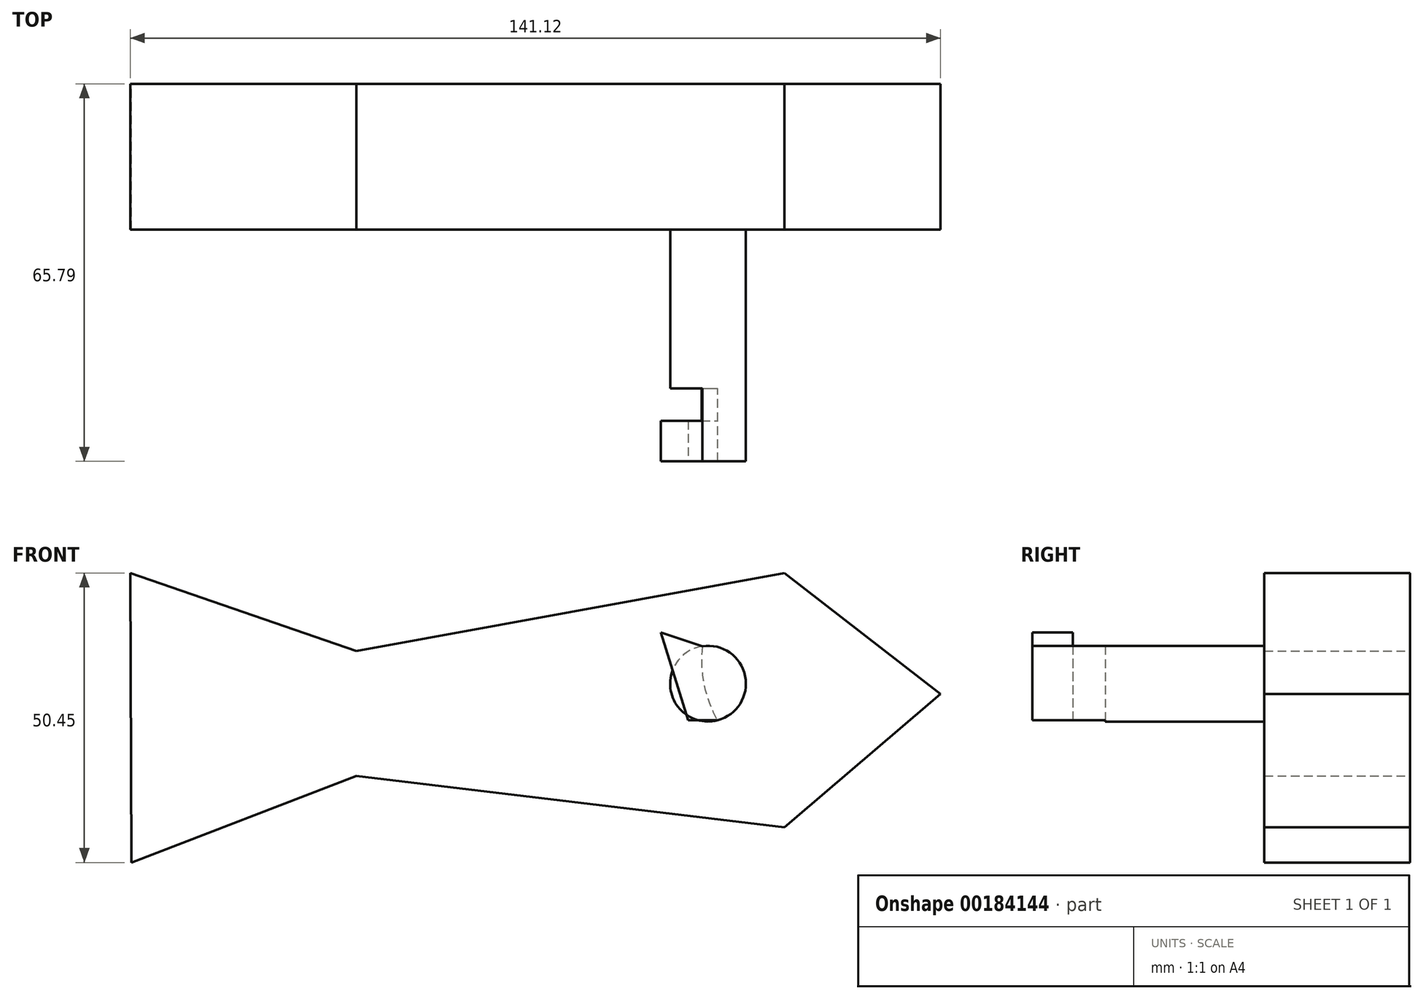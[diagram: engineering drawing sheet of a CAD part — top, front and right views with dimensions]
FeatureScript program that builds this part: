
annotation { "Feature Type Name" : "Feature", "Feature Type Description" : "" }
export const myFeature = defineFeature(function(context is Context, id is Id, definition is map)
    precondition{}
    {
        {
            var Q0;
            Q0=qCreatedBy(makeId("Front.planeOp"),FACE);
            var sketch = newSketch(context, id + "F0", { "sketchPlane" : qUnion([Q0])});
            skLineSegment(sketch, "E0", {"start": v(-76.04, -11.03) * mm, "end": v(-36.69, -24.63) * mm});
            skLineSegment(sketch, "E1", {"start": v(-36.69, -24.63) * mm, "end": v(37.9, -11.03) * mm});
            skLineSegment(sketch, "E2", {"start": v(37.9, -11.03) * mm, "end": v(65.08, -32.1) * mm});
            skLineSegment(sketch, "E3", {"start": v(65.08, -32.1) * mm, "end": v(37.9, -55.37) * mm});
            skLineSegment(sketch, "E4", {"start": v(37.9, -55.37) * mm, "end": v(-36.69, -46.38) * mm});
            skLineSegment(sketch, "E5", {"start": v(-36.69, -46.38) * mm, "end": v(-75.87, -61.48) * mm});
            skLineSegment(sketch, "E6", {"start": v(-76.04, -11.03) * mm, "end": v(-75.87, -61.48) * mm});
            skCircle(sketch, "E7", {"center": v(26.42, -32.28) * mm, "radius": 4.76 * mm});
            skSolve(sketch);
        }
        {
            var Q0;
            Q0=makeQuery(id+"F0.imprint","IMPRINT",FACE,{"disambiguationData":[TD([[makeQuery(id+"F0.imprint","IMPRINT",EDGE,{"derivedFrom":sQuery(id+"F0.wireOp",EDGE,"E0")}),-1.0]])]});
            var Q1;
            Q1=makeQuery(id+"F0.imprint","IMPRINT",FACE,{"disambiguationData":[TD([[makeQuery(id+"F0.imprint","IMPRINT",EDGE,{"derivedFrom":sQuery(id+"F0.wireOp",EDGE,"E7")}),1.0]])]});
            extrude(context, id + "F1", {"entities" : qUnion([Q0, Q1]), "depth" : 25.4 * mm});
        }
        {
            var Q0;
            Q0=makeQuery(id+"F1.opExtrude","CAP_FACE",FACE,{"disambiguationData":[OSD([sQuery(id+"F0.wireOp",EDGE,"E0"),sQuery(id+"F0.wireOp",EDGE,"E1"),sQuery(id+"F0.wireOp",EDGE,"E2"),sQuery(id+"F0.wireOp",EDGE,"E3"),sQuery(id+"F0.wireOp",EDGE,"E4"),sQuery(id+"F0.wireOp",EDGE,"E5"),sQuery(id+"F0.wireOp",EDGE,"E6")])],"isStart":false});
            var sketch = newSketch(context, id + "F2", { "sketchPlane" : qUnion([Q0])});
            skPoint(sketch, "E8.first.point", {"position": v(20.26, -28.29) * mm});
            skPoint(sketch, "E8.second.point", {"position": v(35, -35.2) * mm});
            skPoint(sketch, "E8.third.point", {"position": v(33.42, -27.48) * mm});
            skCircle(sketch, "E9", {"center": v(24.57, -30.3) * mm, "radius": 6.6 * mm});
            skSolve(sketch);
        }
        {
            var Q0;
            Q0=makeQuery(id+"F2.imprint","IMPRINT",FACE,{"disambiguationData":[TD([[makeQuery(id+"F2.imprint","IMPRINT",EDGE,{"derivedFrom":sQuery(id+"F2.wireOp",EDGE,"E9")}),1.0]])]});
            var Q1;
            Q1=sQuery(id+"F2.wireOp",EDGE,"E9");
            extrude(context, id + "F3", {"entities" : qUnion([Q0]), "surfaceEntities" : qUnion([Q1]), "depth" : 27.7 * mm});
        }
        {
            var Q0;
            Q0=makeQuery(id+"F3.opExtrude","CAP_FACE",FACE,{"disambiguationData":[OSD([sQuery(id+"F2.wireOp",EDGE,"E9")])],"isStart":false});
            var sketch = newSketch(context, id + "F4", { "sketchPlane" : qUnion([Q0])});
            skArc(sketch, "E10", {"start": v(23.59, -23.77) * mm, "mid": v(23.87, -30.44) * mm, "end": v(26.23, -36.7) * mm});
            skSolve(sketch);
        }
        {
            var Q0;
            {var subQ0=sQuery(id+"F4.wireOp",EDGE,"E10");Q0=makeQuery(id+"F4.imprint","IMPRINT",FACE,{"disambiguationData":[TD([[makeQuery(id+"F4.imprint","IMPRINT",EDGE,{"derivedFrom":subQ0}),1.0]])]});}
            extrude(context, id + "F5", {"entities" : qUnion([Q0]), "operationType" : NewBodyOperationType.ADD, "depth" : 12.7 * mm});
        }
        {
            var Q0;
            Q0=makeQuery(id+"F5.opExtrude","CAP_FACE",FACE,{"disambiguationData":[OSD([sQuery(id+"F2.wireOp",EDGE,"E9"),sQuery(id+"F4.wireOp",EDGE,"E10")])],"isStart":false});
            var sketch = newSketch(context, id + "F6", { "sketchPlane" : qUnion([Q0])});
            skLineSegment(sketch, "E11", {"start": v(23.59, -23.77) * mm, "end": v(16.36, -21.35) * mm});
            skLineSegment(sketch, "E12", {"start": v(16.36, -21.35) * mm, "end": v(21.1, -36.7) * mm});
            skLineSegment(sketch, "E13", {"start": v(21.1, -36.7) * mm, "end": v(26.23, -36.7) * mm});
            skSolve(sketch);
        }
        {
            var Q0;
            Q0=makeQuery(id+"F6.imprint","IMPRINT",FACE,{"disambiguationData":[TD([[makeQuery(id+"F6.imprint","IMPRINT",EDGE,{"derivedFrom":sQuery(id+"F6.wireOp",EDGE,"E11")}),1.0]])]});
            extrude(context, id + "F7", {"entities" : qUnion([Q0]), "operationType" : NewBodyOperationType.ADD, "oppositeDirection" : true, "depth" : 7.04 * mm});
        }
    });
